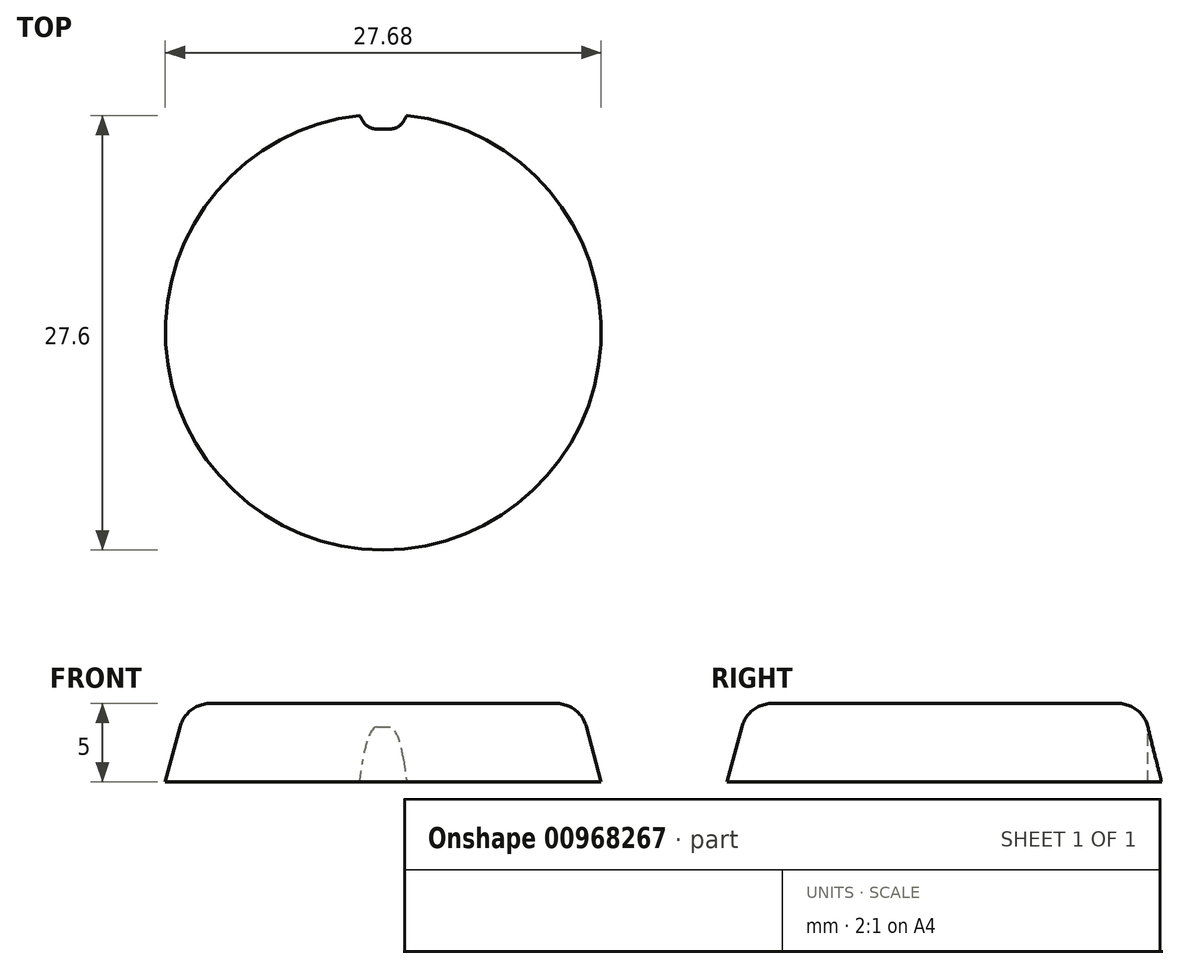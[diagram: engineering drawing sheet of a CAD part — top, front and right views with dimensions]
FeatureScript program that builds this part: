
annotation { "Feature Type Name" : "Feature", "Feature Type Description" : "" }
export const myFeature = defineFeature(function(context is Context, id is Id, definition is map)
    precondition{}
    {
        {
            var Q0;
            Q0=qCreatedBy(makeId("Top.planeOp"),FACE);
            var sketch = newSketch(context, id + "F0", { "sketchPlane" : qUnion([Q0])});
            skCircle(sketch, "E0", {"center": v(0, 0) * mm, "radius": 12.5 * mm});
            skSolve(sketch);
        }
        {
            var Q0;
            Q0=makeQuery(id+"F0.imprint","IMPRINT",FACE,{"disambiguationData":[TD([[makeQuery(id+"F0.imprint","IMPRINT",EDGE,{"derivedFrom":sQuery(id+"F0.wireOp",EDGE,"E0")}),1.0]])]});
            extrude(context, id + "F1", {"entities" : qUnion([Q0]), "oppositeDirection" : true, "depth" : 5 * mm, "offsetDistance" : 25 * mm, "hasDraft" : true, "draftAngle" : 15 * degree});
        }
        {
            var Q0;
            Q0=makeQuery(id+"F1.opExtrude","CAP_EDGE",EDGE,{"disambiguationData":[OSD([sQuery(id+"F0.wireOp",EDGE,"E0")])],"isStart":true});
            fillet(context, id + "F2", {"entities" : qUnion([Q0]), "radius" : 2 * mm, "tangentPropagation" : true, "allowEdgeOverflow" : false});
        }
        {
            var Q0;
            Q0=qCreatedBy(makeId("Top.planeOp"),FACE);
            var sketch = newSketch(context, id + "F3", { "sketchPlane" : qUnion([Q0])});
            skLineSegment(sketch, "E1", {"start": v(-1.5, 13.76) * mm, "end": v(-1, 12.9) * mm});
            skLineSegment(sketch, "E2", {"start": v(-1, 12.9) * mm, "end": v(1, 12.9) * mm});
            skLineSegment(sketch, "E3", {"start": v(1, 12.9) * mm, "end": v(1.5, 13.76) * mm});
            skArc(sketch, "E4", {"start": v(1.5, 13.76) * mm, "mid": v(0, 13.84) * mm, "end": v(-1.5, 13.76) * mm});
            skSolve(sketch);
        }
        {
            var Q0;
            Q0=makeQuery(id+"F3.imprint","IMPRINT",FACE,{"disambiguationData":[TD([[makeQuery(id+"F3.imprint","IMPRINT",EDGE,{"derivedFrom":sQuery(id+"F3.wireOp",EDGE,"E1")}),1.0]])]});
            extrude(context, id + "F4", {"entities" : qUnion([Q0]), "operationType" : NewBodyOperationType.REMOVE, "oppositeDirection" : true, "depth" : 25 * mm, "offsetDistance" : 25 * mm});
        }
        {
            var Q0;
            Q0=makeQuery(id+"F4.boolean.opBoolean","COPY",EDGE,{"derivedFrom":makeQuery(id+"F4.opExtrude","SWEPT_EDGE",EDGE,{"disambiguationData":[OSD([sQuery(id+"F3.wireOp",EDGE,"E1"),sQuery(id+"F3.wireOp",EDGE,"E2")])]})});
            var Q1;
            Q1=makeQuery(id+"F4.boolean.opBoolean","COPY",EDGE,{"derivedFrom":makeQuery(id+"F4.opExtrude","SWEPT_EDGE",EDGE,{"disambiguationData":[OSD([sQuery(id+"F3.wireOp",EDGE,"E2"),sQuery(id+"F3.wireOp",EDGE,"E3")])]})});
            fillet(context, id + "F5", {"entities" : qUnion([Q0, Q1]), "radius" : 1 * mm, "tangentPropagation" : true, "allowEdgeOverflow" : false});
        }
    });
